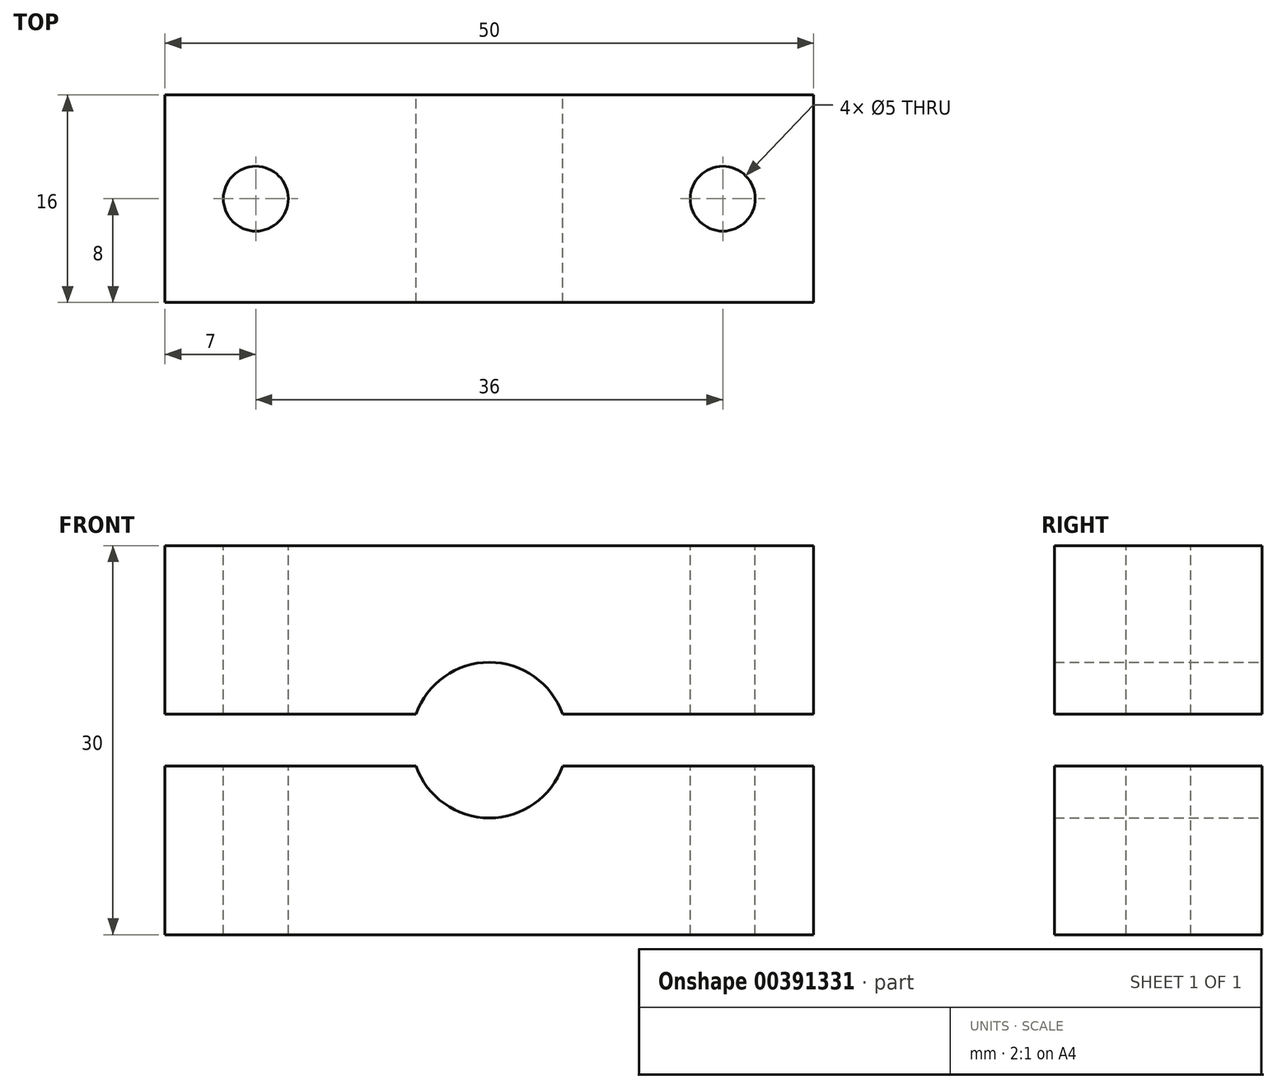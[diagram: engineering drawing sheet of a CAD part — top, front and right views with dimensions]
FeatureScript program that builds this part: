
annotation { "Feature Type Name" : "Feature", "Feature Type Description" : "" }
export const myFeature = defineFeature(function(context is Context, id is Id, definition is map)
    precondition{}
    {
        {
            var Q0;
            Q0=qCreatedBy(makeId("Front.planeOp"),FACE);
            var sketch = newSketch(context, id + "F0", { "sketchPlane" : qUnion([Q0])});
            skLineSegment(sketch, "E0.bottom", {"start": v(0, 0) * mm, "end": v(50, 0) * mm});
            skLineSegment(sketch, "E0.top", {"start": v(0, 13) * mm, "end": v(50, 13) * mm});
            skLineSegment(sketch, "E0.left", {"start": v(0, 0) * mm, "end": v(0, 13) * mm});
            skLineSegment(sketch, "E0.right", {"start": v(50, 0) * mm, "end": v(50, 13) * mm});
            skLineSegment(sketch, "E1.bottom", {"start": v(0, 17) * mm, "end": v(50, 17) * mm});
            skLineSegment(sketch, "E1.top", {"start": v(0, 30) * mm, "end": v(50, 30) * mm});
            skLineSegment(sketch, "E1.left", {"start": v(0, 17) * mm, "end": v(0, 30) * mm});
            skLineSegment(sketch, "E1.right", {"start": v(50, 17) * mm, "end": v(50, 30) * mm});
            skCircle(sketch, "E2", {"center": v(25, 15) * mm, "radius": 6 * mm});
            skSolve(sketch);
        }
        {
            var Q0;
            Q0=makeQuery(id+"F0.imprint","IMPRINT",FACE,{"disambiguationData":[TD([[makeQuery(id+"F0.imprint","IMPRINT",EDGE,{"derivedFrom":sQuery(id+"F0.wireOp",EDGE,"E1.top")}),-1.0]])]});
            var Q1;
            Q1=makeQuery(id+"F0.imprint","IMPRINT",FACE,{"disambiguationData":[TD([[makeQuery(id+"F0.imprint","IMPRINT",EDGE,{"derivedFrom":sQuery(id+"F0.wireOp",EDGE,"E0.bottom")}),1.0]])]});
            extrude(context, id + "F1", {"entities" : qUnion([Q0, Q1]), "endBound" : BoundingType.SYMMETRIC, "depth" : 16 * mm});
        }
        {
            var Q0;
            Q0=makeQuery(id+"F1.opExtrude","SWEPT_FACE",FACE,{"disambiguationData":[OSD([sQuery(id+"F0.wireOp",EDGE,"E1.top")])]});
            var sketch = newSketch(context, id + "F2", { "sketchPlane" : qUnion([Q0])});
            skCircle(sketch, "E3", {"center": v(7, 0) * mm, "radius": 2.5 * mm});
            skCircle(sketch, "E4", {"center": v(43, 0) * mm, "radius": 2.5 * mm});
            skSolve(sketch);
        }
        {
            var Q0;
            Q0=qSketchRegion(id+"F2",true);
            extrude(context, id + "F3", {"entities" : qUnion([Q0]), "operationType" : NewBodyOperationType.REMOVE, "oppositeDirection" : true, "depth" : 50 * mm});
        }
    });
